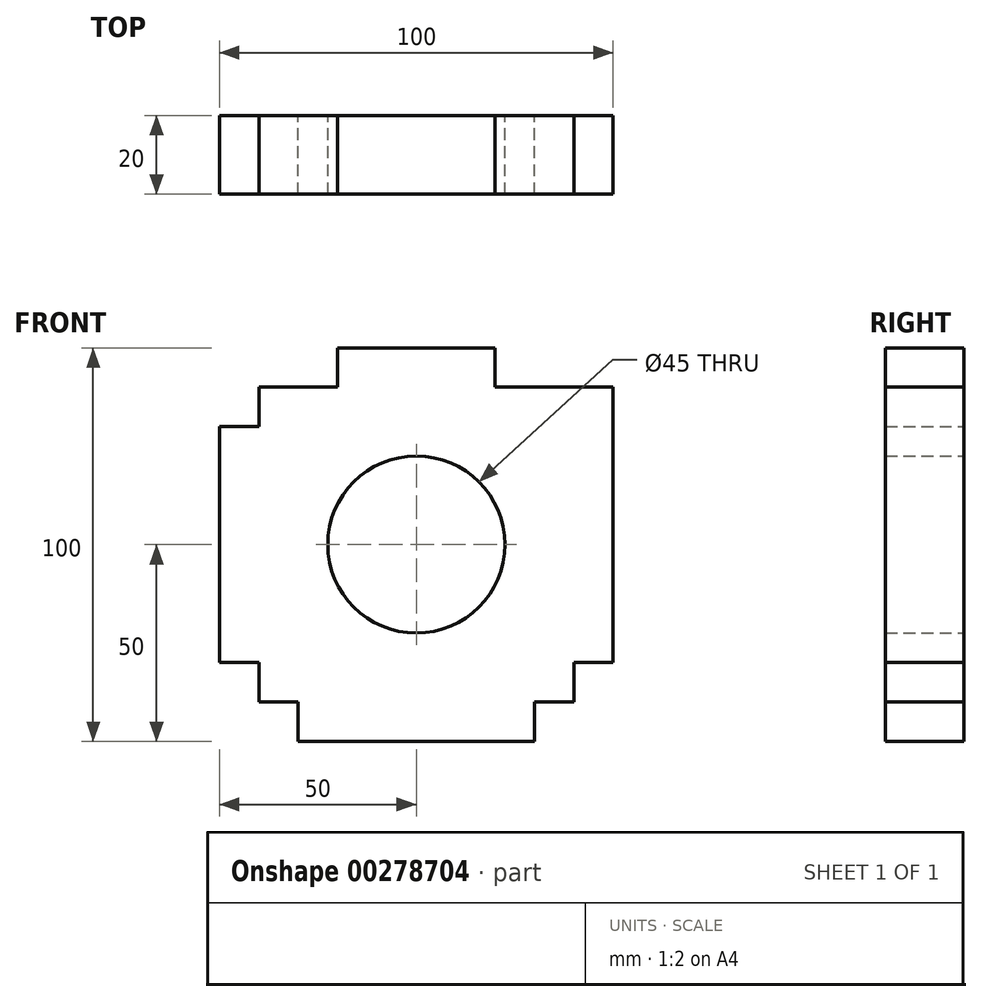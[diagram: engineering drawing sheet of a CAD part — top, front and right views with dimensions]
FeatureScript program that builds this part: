
annotation { "Feature Type Name" : "Feature", "Feature Type Description" : "" }
export const myFeature = defineFeature(function(context is Context, id is Id, definition is map)
    precondition{}
    {
        {
            var Q0;
            Q0=qCreatedBy(makeId("Front.planeOp"),FACE);
            var sketch = newSketch(context, id + "F0", { "sketchPlane" : qUnion([Q0])});
            skLineSegment(sketch, "E0.bottom", {"start": v(-40, 50) * mm, "end": v(39.98, 50) * mm});
            skLineSegment(sketch, "E0.top", {"start": v(-30, -50) * mm, "end": v(30, -50) * mm});
            skLineSegment(sketch, "E0.left", {"start": v(-50, 40) * mm, "end": v(-50, -30) * mm});
            skLineSegment(sketch, "E0.right", {"start": v(50, 39.98) * mm, "end": v(50, -30) * mm});
            skPoint(sketch, "E1.visualSharp", {"position": v(-50, 50) * mm});
            skLineSegment(sketch, "E1.filletArc", {"start": v(-50, 50) * mm, "end": v(-50, 50) * mm});
            skPoint(sketch, "E2.visualSharp", {"position": v(50, 50) * mm});
            skLineSegment(sketch, "E2.filletArc", {"start": v(50, 50) * mm, "end": v(50, 50) * mm});
            skPoint(sketch, "E3.visualSharp", {"position": v(50, -50) * mm});
            skLineSegment(sketch, "E3.filletArc", {"start": v(50, -50) * mm, "end": v(50, -50) * mm});
            skPoint(sketch, "E4.visualSharp", {"position": v(-50, -50) * mm});
            skLineSegment(sketch, "E4.filletArc", {"start": v(-50, -50) * mm, "end": v(-50, -50) * mm});
            skCircle(sketch, "E5", {"center": v(0, 0) * mm, "radius": 22.5 * mm});
            skLineSegment(sketch, "E6.top", {"start": v(-50, 40) * mm, "end": v(-40, 40) * mm});
            skLineSegment(sketch, "E6.right", {"start": v(-40, 50) * mm, "end": v(-40, 40) * mm});
            skLineSegment(sketch, "E7.filletArc", {"start": v(81.62, -53.83) * mm, "end": v(81.62, -53.83) * mm});
            skLineSegment(sketch, "E8.bottom", {"start": v(40, -40) * mm, "end": v(40, -40) * mm});
            skLineSegment(sketch, "E8.left", {"start": v(40, -40) * mm, "end": v(40, -40) * mm});
            skPoint(sketch, "E9.visualSharp", {"position": v(49.98, 49.98) * mm});
            skLineSegment(sketch, "E9.filletArc", {"start": v(54.13, 50.27) * mm, "end": v(54.13, 50.27) * mm});
            skLineSegment(sketch, "E10.top", {"start": v(39.98, 39.98) * mm, "end": v(50, 39.98) * mm});
            skLineSegment(sketch, "E10.left", {"start": v(39.98, 50) * mm, "end": v(39.98, 39.98) * mm});
            skLineSegment(sketch, "E11.bottom", {"start": v(-40, 40) * mm, "end": v(-30, 40) * mm});
            skLineSegment(sketch, "E11.top", {"start": v(-40, 30) * mm, "end": v(-30, 30) * mm});
            skLineSegment(sketch, "E11.left", {"start": v(-40, 40) * mm, "end": v(-40, 30) * mm});
            skLineSegment(sketch, "E11.right", {"start": v(-30, 40) * mm, "end": v(-30, 30) * mm});
            skLineSegment(sketch, "E12.bottom", {"start": v(-50, 30) * mm, "end": v(-40, 30) * mm});
            skLineSegment(sketch, "E12.top", {"start": v(-50, 20) * mm, "end": v(-40, 20) * mm});
            skLineSegment(sketch, "E12.left", {"start": v(-50, 30) * mm, "end": v(-50, 20) * mm});
            skLineSegment(sketch, "E12.right", {"start": v(-40, 30) * mm, "end": v(-40, 20) * mm});
            skLineSegment(sketch, "E13.bottom", {"start": v(-30, 50) * mm, "end": v(-20, 50) * mm});
            skLineSegment(sketch, "E13.top", {"start": v(-30, 40) * mm, "end": v(-20, 40) * mm});
            skLineSegment(sketch, "E13.left", {"start": v(-30, 50) * mm, "end": v(-30, 40) * mm});
            skLineSegment(sketch, "E13.right", {"start": v(-20, 50) * mm, "end": v(-20, 40) * mm});
            skLineSegment(sketch, "E14.MirrorCS", {"start": v(50, 30) * mm, "end": v(40, 30) * mm});
            skLineSegment(sketch, "E15.MirrorCS", {"start": v(20, 50) * mm, "end": v(20, 40) * mm});
            skLineSegment(sketch, "E16.MirrorCS", {"start": v(30, 50) * mm, "end": v(20, 50) * mm});
            skLineSegment(sketch, "E17.MirrorCS", {"start": v(50, 30) * mm, "end": v(50, 20) * mm});
            skLineSegment(sketch, "E18.MirrorCS", {"start": v(40, 40) * mm, "end": v(30, 40) * mm});
            skLineSegment(sketch, "E19.MirrorCS", {"start": v(40, 30) * mm, "end": v(30, 30) * mm});
            skLineSegment(sketch, "E20.MirrorCS", {"start": v(40, 40) * mm, "end": v(40, 30) * mm});
            skLineSegment(sketch, "E21.MirrorCS", {"start": v(50, 40) * mm, "end": v(40, 40) * mm});
            skLineSegment(sketch, "E22.MirrorCS", {"start": v(50, 20) * mm, "end": v(40, 20) * mm});
            skLineSegment(sketch, "E23.MirrorCS", {"start": v(30, 50) * mm, "end": v(30, 40) * mm});
            skLineSegment(sketch, "E24.MirrorCS", {"start": v(40, 50) * mm, "end": v(40, 40) * mm});
            skLineSegment(sketch, "E25.MirrorCS", {"start": v(40, 30) * mm, "end": v(40, 20) * mm});
            skLineSegment(sketch, "E26.MirrorCS", {"start": v(30, 40) * mm, "end": v(30, 30) * mm});
            skLineSegment(sketch, "E27.MirrorCS", {"start": v(30, 40) * mm, "end": v(20, 40) * mm});
            skLineSegment(sketch, "E28.MirrorCS", {"start": v(-30, -50) * mm, "end": v(-20, -50) * mm});
            skLineSegment(sketch, "E29.MirrorCS", {"start": v(-40, -30) * mm, "end": v(-30, -30) * mm});
            skLineSegment(sketch, "E30.MirrorCS", {"start": v(-50, -20) * mm, "end": v(-40, -20) * mm});
            skLineSegment(sketch, "E31.MirrorCS", {"start": v(-30, -40) * mm, "end": v(-20, -40) * mm});
            skLineSegment(sketch, "E32.MirrorCS", {"start": v(-50, -30) * mm, "end": v(-40, -30) * mm});
            skLineSegment(sketch, "E33.MirrorCS", {"start": v(-50, -30) * mm, "end": v(-50, -20) * mm});
            skLineSegment(sketch, "E34.MirrorCS", {"start": v(-20, -50) * mm, "end": v(-20, -40) * mm});
            skLineSegment(sketch, "E35.MirrorCS", {"start": v(-30, -40) * mm, "end": v(-30, -30) * mm});
            skLineSegment(sketch, "E36.MirrorCS", {"start": v(-40, -30) * mm, "end": v(-40, -20) * mm});
            skLineSegment(sketch, "E37.MirrorCS", {"start": v(-30, -50) * mm, "end": v(-30, -40) * mm});
            skLineSegment(sketch, "E38.MirrorCS", {"start": v(-40, -40) * mm, "end": v(-40, -30) * mm});
            skLineSegment(sketch, "E39.MirrorCS", {"start": v(-40, -40) * mm, "end": v(-30, -40) * mm});
            skPoint(sketch, "E40.MirrorP", {"position": v(49.98, -49.98) * mm});
            skLineSegment(sketch, "E41.MirrorCS", {"start": v(50, -30) * mm, "end": v(40, -30) * mm});
            skLineSegment(sketch, "E42.MirrorCS", {"start": v(50, -20) * mm, "end": v(40, -20) * mm});
            skLineSegment(sketch, "E43.MirrorCS", {"start": v(20, -50) * mm, "end": v(20, -40) * mm});
            skLineSegment(sketch, "E44.MirrorCS", {"start": v(30, -50) * mm, "end": v(30, -40) * mm});
            skLineSegment(sketch, "E45.MirrorCS", {"start": v(40, -40) * mm, "end": v(40, -30) * mm});
            skLineSegment(sketch, "E46.MirrorCS", {"start": v(50, -30) * mm, "end": v(50, -20) * mm});
            skLineSegment(sketch, "E47.MirrorCS", {"start": v(40, -40) * mm, "end": v(39.98, -40) * mm});
            skLineSegment(sketch, "E48.MirrorCS", {"start": v(30, -50) * mm, "end": v(20, -50) * mm});
            skLineSegment(sketch, "E49.MirrorCS", {"start": v(40, -30) * mm, "end": v(40, -20) * mm});
            skLineSegment(sketch, "E50.MirrorCS", {"start": v(30, -40) * mm, "end": v(20, -40) * mm});
            skLineSegment(sketch, "E51.MirrorCS", {"start": v(30, -40) * mm, "end": v(30, -30) * mm});
            skLineSegment(sketch, "E52.MirrorCS", {"start": v(40, -30) * mm, "end": v(30, -30) * mm});
            skLineSegment(sketch, "E53.MirrorCS", {"start": v(40, -40) * mm, "end": v(30, -40) * mm});
            skLineSegment(sketch, "E54.MirrorCS", {"start": v(50, -20) * mm, "end": v(50, 40) * mm});
            skLineSegment(sketch, "E55.MirrorCS", {"start": v(39.98, -50) * mm, "end": v(39.98, -39.98) * mm});
            skPoint(sketch, "E56.orphan", {"position": v(-40, -50) * mm});
            skPoint(sketch, "E57.MirrorCS.start.orphan", {"position": v(-50, -40) * mm});
            skLineSegment(sketch, "E58.trimOffspring", {"start": v(39.98, -50) * mm, "end": v(40, -50) * mm});
            skPoint(sketch, "E59.MirrorCS.start.orphan", {"position": v(40, -50) * mm});
            skLineSegment(sketch, "E60.trimOffspring", {"start": v(50, -39.98) * mm, "end": v(50, -40) * mm});
            skPoint(sketch, "E61.MirrorCS.start.orphan", {"position": v(50, -40) * mm});
            skSolve(sketch);
        }
        {
            var Q0;
            {var subQ0=sQuery(id+"F0.wireOp",EDGE,"E8.left");var subQ1=sQuery(id+"F0.wireOp",EDGE,"E8.bottom");var subQ2=makeQuery(id+"F0.imprint","INTERSECT",VERTEX,{"derivedFrom":[subQ1,subQ0]});Q0=makeQuery(id+"F0.imprint","IMPRINT",FACE,{"disambiguationData":[TD([[makeQuery(id+"F0.imprint","IMPRINT",EDGE,{"disambiguationData":[TD([[subQ2,-1.0]])],"derivedFrom":subQ1}),-1.0]])]});}
            var Q1;
            {var subQ0=sQuery(id+"F0.wireOp",EDGE,"E10.left");var subQ1=sQuery(id+"F0.wireOp",EDGE,"E10.top");var subQ2=makeQuery(id+"F0.imprint","INTERSECT",VERTEX,{"derivedFrom":[subQ1,subQ0]});Q1=makeQuery(id+"F0.imprint","IMPRINT",FACE,{"disambiguationData":[TD([[makeQuery(id+"F0.imprint","IMPRINT",EDGE,{"disambiguationData":[TD([[subQ2,-1.0]])],"derivedFrom":subQ1}),1.0]])]});}
            var Q2;
            {var subQ0=sQuery(id+"F0.wireOp",EDGE,"E0.top");Q2=makeQuery(id+"F0.imprint","IMPRINT",FACE,{"disambiguationData":[TD([[makeQuery(id+"F0.imprint","IMPRINT",EDGE,{"derivedFrom":subQ0}),1.0]])]});}
            var Q3;
            {var subQ0=sQuery(id+"F0.wireOp",EDGE,"E0.right");Q3=makeQuery(id+"F0.imprint","IMPRINT",FACE,{"disambiguationData":[TD([[makeQuery(id+"F0.imprint","IMPRINT",EDGE,{"derivedFrom":subQ0}),-1.0]])]});}
            var Q4;
            Q4=makeQuery(id+"F0.imprint","IMPRINT",FACE,{"disambiguationData":[TD([[makeQuery(id+"F0.imprint","IMPRINT",EDGE,{"derivedFrom":sQuery(id+"F0.wireOp",EDGE,"E12.bottom")}),-1.0]])]});
            var Q5;
            Q5=makeQuery(id+"F0.imprint","IMPRINT",FACE,{"disambiguationData":[TD([[makeQuery(id+"F0.imprint","IMPRINT",EDGE,{"derivedFrom":sQuery(id+"F0.wireOp",EDGE,"E13.bottom")}),-1.0]])]});
            var Q6;
            Q6=makeQuery(id+"F0.imprint","IMPRINT",FACE,{"disambiguationData":[TD([[makeQuery(id+"F0.imprint","IMPRINT",EDGE,{"derivedFrom":sQuery(id+"F0.wireOp",EDGE,"E16.MirrorCS")}),1.0]])]});
            var Q7;
            {var subQ0=sQuery(id+"F0.wireOp",EDGE,"E22.MirrorCS");Q7=makeQuery(id+"F0.imprint","IMPRINT",FACE,{"disambiguationData":[TD([[makeQuery(id+"F0.imprint","IMPRINT",EDGE,{"derivedFrom":subQ0}),-1.0]])]});}
            var Q8;
            Q8=makeQuery(id+"F0.imprint","IMPRINT",FACE,{"disambiguationData":[TD([[makeQuery(id+"F0.imprint","IMPRINT",EDGE,{"derivedFrom":sQuery(id+"F0.wireOp",EDGE,"E30.MirrorCS")}),-1.0]])]});
            var Q9;
            Q9=makeQuery(id+"F0.imprint","IMPRINT",FACE,{"disambiguationData":[TD([[makeQuery(id+"F0.imprint","IMPRINT",EDGE,{"derivedFrom":sQuery(id+"F0.wireOp",EDGE,"E31.MirrorCS")}),-1.0]])]});
            var Q10;
            Q10=makeQuery(id+"F0.imprint","IMPRINT",FACE,{"disambiguationData":[TD([[makeQuery(id+"F0.imprint","IMPRINT",EDGE,{"derivedFrom":sQuery(id+"F0.wireOp",EDGE,"E11.bottom")}),-1.0]])]});
            var Q11;
            Q11=makeQuery(id+"F0.imprint","IMPRINT",FACE,{"disambiguationData":[TD([[makeQuery(id+"F0.imprint","IMPRINT",EDGE,{"derivedFrom":sQuery(id+"F0.wireOp",EDGE,"E29.MirrorCS")}),-1.0]])]});
            var Q12;
            {var subQ1=sQuery(id+"F0.wireOp",EDGE,"E8.left");var subQ9=sQuery(id+"F0.wireOp",EDGE,"E8.bottom");var subQ10=makeQuery(id+"F0.imprint","INTERSECT",VERTEX,{"derivedFrom":[subQ9,subQ1]});Q12=makeQuery(id+"F0.imprint","IMPRINT",FACE,{"disambiguationData":[TD([[makeQuery(id+"F0.imprint","IMPRINT",EDGE,{"disambiguationData":[TD([[subQ10,-1.0]])],"derivedFrom":subQ9}),1.0]])]});}
            var Q13;
            {var subQ7=sQuery(id+"F0.wireOp",EDGE,"E19.MirrorCS");Q13=makeQuery(id+"F0.imprint","IMPRINT",FACE,{"disambiguationData":[TD([[makeQuery(id+"F0.imprint","IMPRINT",EDGE,{"derivedFrom":subQ7}),-1.0]])]});}
            var Q14;
            {var subQ0=sQuery(id+"F0.wireOp",EDGE,"E44.MirrorCS");Q14=makeQuery(id+"F0.imprint","IMPRINT",FACE,{"disambiguationData":[TD([[makeQuery(id+"F0.imprint","IMPRINT",EDGE,{"derivedFrom":subQ0}),1.0]])]});}
            var Q15;
            {var subQ0=sQuery(id+"F0.wireOp",EDGE,"E41.MirrorCS");Q15=makeQuery(id+"F0.imprint","IMPRINT",FACE,{"disambiguationData":[TD([[makeQuery(id+"F0.imprint","IMPRINT",EDGE,{"derivedFrom":subQ0}),-1.0]])]});}
            var Q16;
            {var subQ8=sQuery(id+"F0.wireOp",EDGE,"E51.MirrorCS");Q16=makeQuery(id+"F0.imprint","IMPRINT",FACE,{"disambiguationData":[TD([[makeQuery(id+"F0.imprint","IMPRINT",EDGE,{"derivedFrom":subQ8}),-1.0]])]});}
            var Q17;
            Q17=makeQuery(id+"F0.imprint","IMPRINT",FACE,{"disambiguationData":[TD([[makeQuery(id+"F0.imprint","IMPRINT",EDGE,{"derivedFrom":sQuery(id+"F0.wireOp",EDGE,"E11.top")}),-1.0]])]});
            extrude(context, id + "F1", {"entities" : qUnion([Q0, Q1, Q2, Q3, Q4, Q5, Q6, Q7, Q8, Q9, Q10, Q11, Q12, Q13, Q14, Q15, Q16, Q17]), "depth" : 20 * mm});
        }
    });
